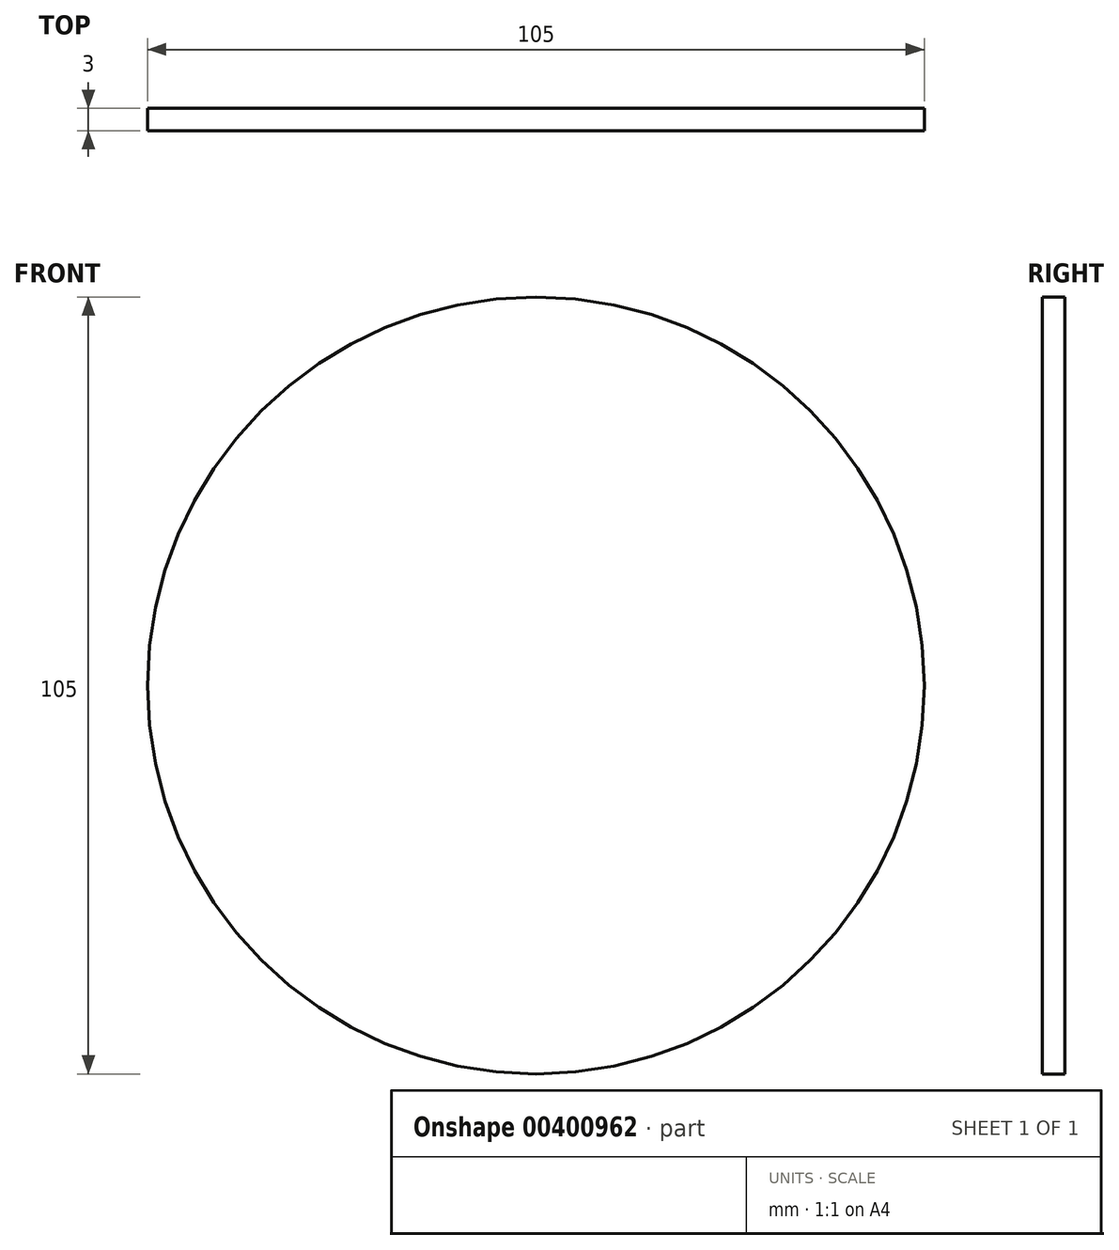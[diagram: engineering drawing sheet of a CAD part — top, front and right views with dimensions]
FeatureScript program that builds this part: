
annotation { "Feature Type Name" : "Feature", "Feature Type Description" : "" }
export const myFeature = defineFeature(function(context is Context, id is Id, definition is map)
    precondition{}
    {
        {
            var Q0;
            Q0=qCreatedBy(makeId("Front.planeOp"),FACE);
            var sketch = newSketch(context, id + "F0", { "sketchPlane" : qUnion([Q0])});
            skCircle(sketch, "E0", {"center": v(0, 0) * mm, "radius": 52.5 * mm});
            skSolve(sketch);
        }
        {
            var Q0;
            Q0 = qSketchRegion(id + "F0", true);
            extrude(context, id + "F1", {"entities" : qUnion([Q0]), "depth" : 3 * mm});
        }
    });
